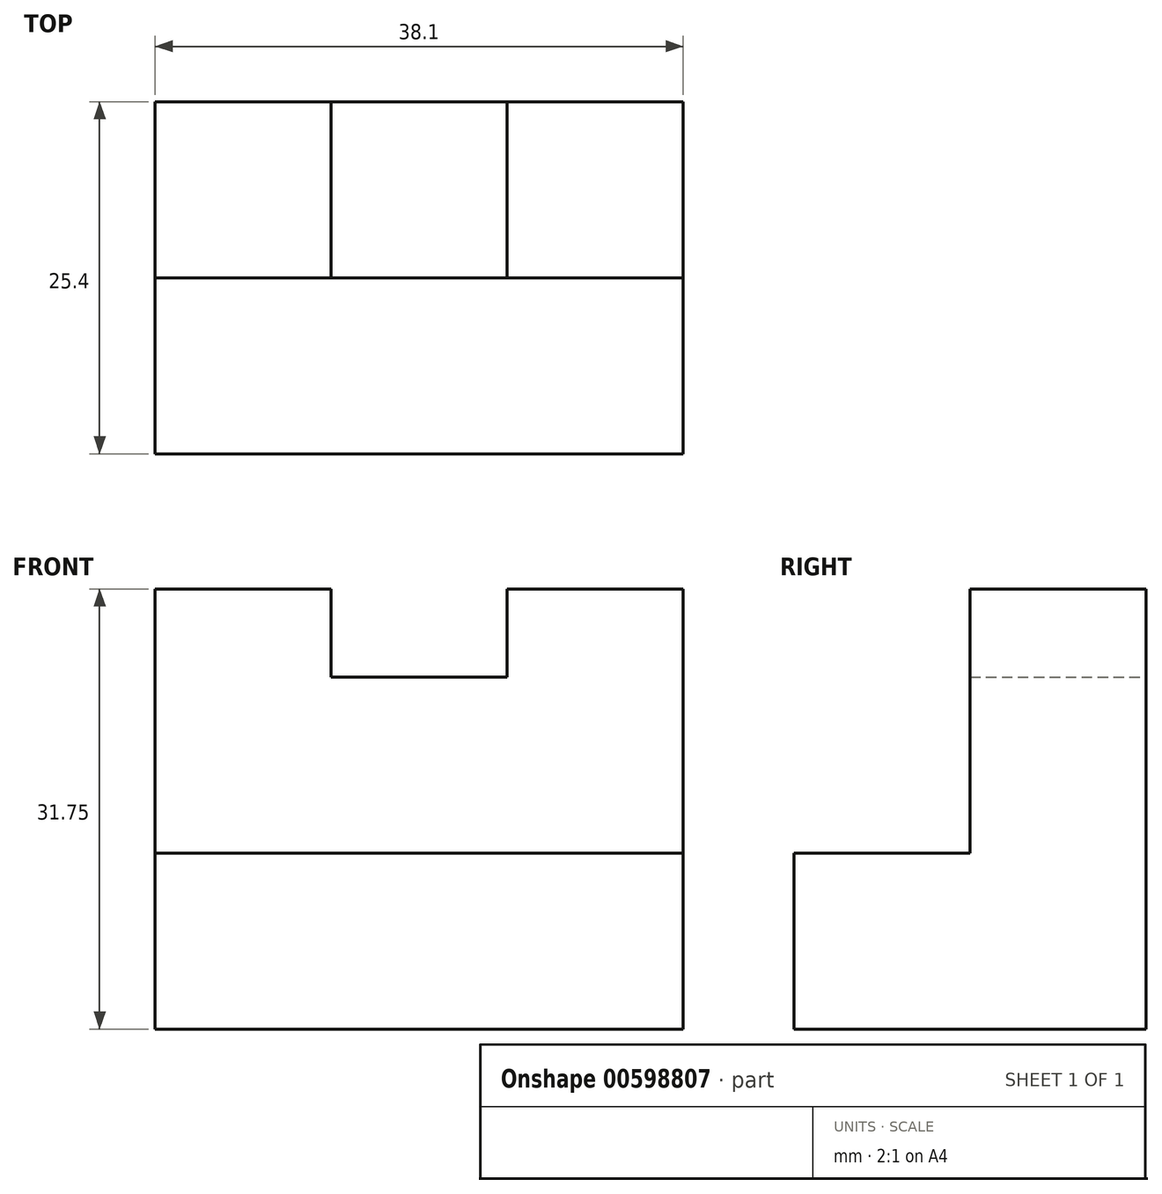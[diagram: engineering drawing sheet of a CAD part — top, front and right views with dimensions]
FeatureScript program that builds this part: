
annotation { "Feature Type Name" : "Feature", "Feature Type Description" : "" }
export const myFeature = defineFeature(function(context is Context, id is Id, definition is map)
    precondition{}
    {
        {
            var Q0;
            Q0=qCreatedBy(makeId("Front.planeOp"),FACE);
            var sketch = newSketch(context, id + "F0", { "sketchPlane" : qUnion([Q0])});
            skLineSegment(sketch, "E0", {"start": v(0, 0) * mm, "end": v(0, 12.7) * mm});
            skLineSegment(sketch, "E1", {"start": v(0, 12.7) * mm, "end": v(38.1, 12.7) * mm});
            skLineSegment(sketch, "E2", {"start": v(38.1, 12.7) * mm, "end": v(38.1, 0) * mm});
            skLineSegment(sketch, "E3", {"start": v(38.1, 0) * mm, "end": v(0, 0) * mm});
            skLineSegment(sketch, "E4", {"start": v(0, 12.7) * mm, "end": v(0, 31.75) * mm});
            skLineSegment(sketch, "E5", {"start": v(0, 31.75) * mm, "end": v(12.7, 31.75) * mm});
            skLineSegment(sketch, "E6", {"start": v(12.7, 31.75) * mm, "end": v(12.7, 25.4) * mm});
            skLineSegment(sketch, "E7", {"start": v(12.7, 25.4) * mm, "end": v(25.4, 25.4) * mm});
            skLineSegment(sketch, "E8", {"start": v(25.4, 25.4) * mm, "end": v(25.4, 31.75) * mm});
            skLineSegment(sketch, "E9", {"start": v(25.4, 31.75) * mm, "end": v(38.1, 31.75) * mm});
            skLineSegment(sketch, "E10", {"start": v(38.1, 31.75) * mm, "end": v(38.1, 10.6) * mm});
            skSolve(sketch);
        }
        {
            var Q0;
            Q0=makeQuery(id+"F0.imprint","IMPRINT",FACE,{"disambiguationData":[TD([[makeQuery(id+"F0.imprint","IMPRINT",EDGE,{"derivedFrom":sQuery(id+"F0.wireOp",EDGE,"E0")}),-1.0]])]});
            extrude(context, id + "F1", {"entities" : qUnion([Q0]), "depth" : 25.4 * mm, "offsetDistance" : 25.4 * mm});
        }
        {
            var Q0;
            Q0 = qSketchRegion(id + "F0", true);
            extrude(context, id + "F2", {"entities" : qUnion([Q0]), "operationType" : NewBodyOperationType.ADD, "depth" : 12.7 * mm, "offsetDistance" : 25.4 * mm});
        }
    });
